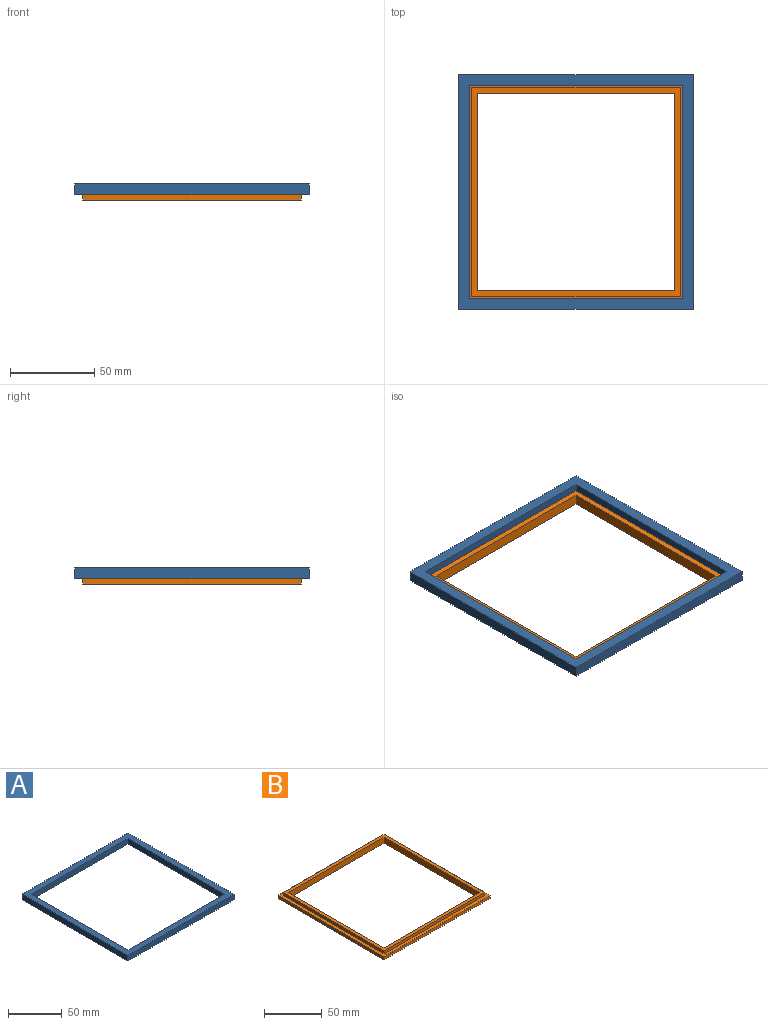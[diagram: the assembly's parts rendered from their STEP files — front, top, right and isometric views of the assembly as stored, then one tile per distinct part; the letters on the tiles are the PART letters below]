
ASSEMBLY  parts=2 mates=1
PART A: 10 faces, bbox 139.7x139.7x6.4 mm
  f0: plane 127x6.35mm, normal (0,1,0), area 806.5mm2, adj f1,f7,f8,f9
  f1: plane 127x6.35mm, normal (1,0,0), area 806.5mm2, adj f0,f2,f8,f9
  f2: plane 127x6.35mm, normal (0,-1,0), area 806.5mm2, adj f1,f7,f8,f9
  f3: plane 139.7x6.35mm, normal (0,1,0), area 887.1mm2, adj f4,f6,f8,f9
  f4: plane 139.7x6.35mm, normal (-1,0,0), area 887.1mm2, adj f3,f5,f8,f9
  f5: plane 139.7x6.35mm, normal (0,-1,0), area 887.1mm2, adj f4,f6,f8,f9
  f6: plane 139.7x6.35mm, normal (1,0,0), area 887.1mm2, adj f3,f5,f8,f9
  f7: plane 127x6.35mm, normal (-1,0,0), area 806.5mm2, adj f0,f2,f8,f9
  f8: plane 139.7x139.7mm, normal (0,0,1), area 3387.1mm2, adj f0,f1,f2,f3,f4,f5,f6,f7
  f9: plane 139.7x139.7mm, normal (0,0,-1), area 3387.1mm2, adj f0,f1,f2,f3,f4,f5,f6,f7
PART B: 15 faces, bbox 130.2x130.2x6.4 mm
  f0: plane 117.48x6.35mm, normal (0,1,0), area 746mm2, adj f1,f7,f9,f14
  f1: plane 117.48x6.35mm, normal (1,0,0), area 746mm2, adj f0,f2,f9,f14
  f2: plane 117.48x6.35mm, normal (0,-1,0), area 746mm2, adj f1,f7,f9,f14
  f3: plane 130.18x3.18mm, normal (0,1,0), area 413.3mm2, adj f4,f6,f8,f9
  f4: plane 130.18x3.18mm, normal (-1,0,0), area 413.3mm2, adj f3,f5,f8,f9
  f5: plane 130.18x3.18mm, normal (0,-1,0), area 413.3mm2, adj f4,f6,f8,f9
  f6: plane 130.18x3.18mm, normal (1,0,0), area 413.3mm2, adj f3,f5,f8,f9
  f7: plane 117.48x6.35mm, normal (-1,0,0), area 746mm2, adj f0,f2,f9,f14
  f8: plane 130.18x130.18mm, normal (0,0,1), area 1612.9mm2, adj f3,f4,f5,f6,f10,f11,f12,f13
  f9: plane 130.18x130.18mm, normal (0,0,-1), area 3145.2mm2, adj f0,f1,f2,f3,f4,f5,f6,f7
  f10: plane 123.83x3.18mm, normal (0,1,0), area 393.1mm2, adj f8,f11,f13,f14
  f11: plane 123.83x3.18mm, normal (-1,0,0), area 393.1mm2, adj f8,f10,f12,f14
  f12: plane 123.83x3.18mm, normal (0,-1,0), area 393.1mm2, adj f8,f11,f13,f14
  f13: plane 123.83x3.18mm, normal (1,0,0), area 393.1mm2, adj f8,f10,f12,f14
  f14: plane 123.83x123.83mm, normal (0,0,1), area 1532.3mm2, adj f0,f1,f2,f7,f10,f11,f12,f13
PLACE A t=(25.82,23.13,-35.63)mm
PLACE B t=(25.82,23.13,-38.81)mm
MATE planar B.f8 <-> A.f9  axis (0,0,1) through (-36.1,85.04,-35.63)mm
